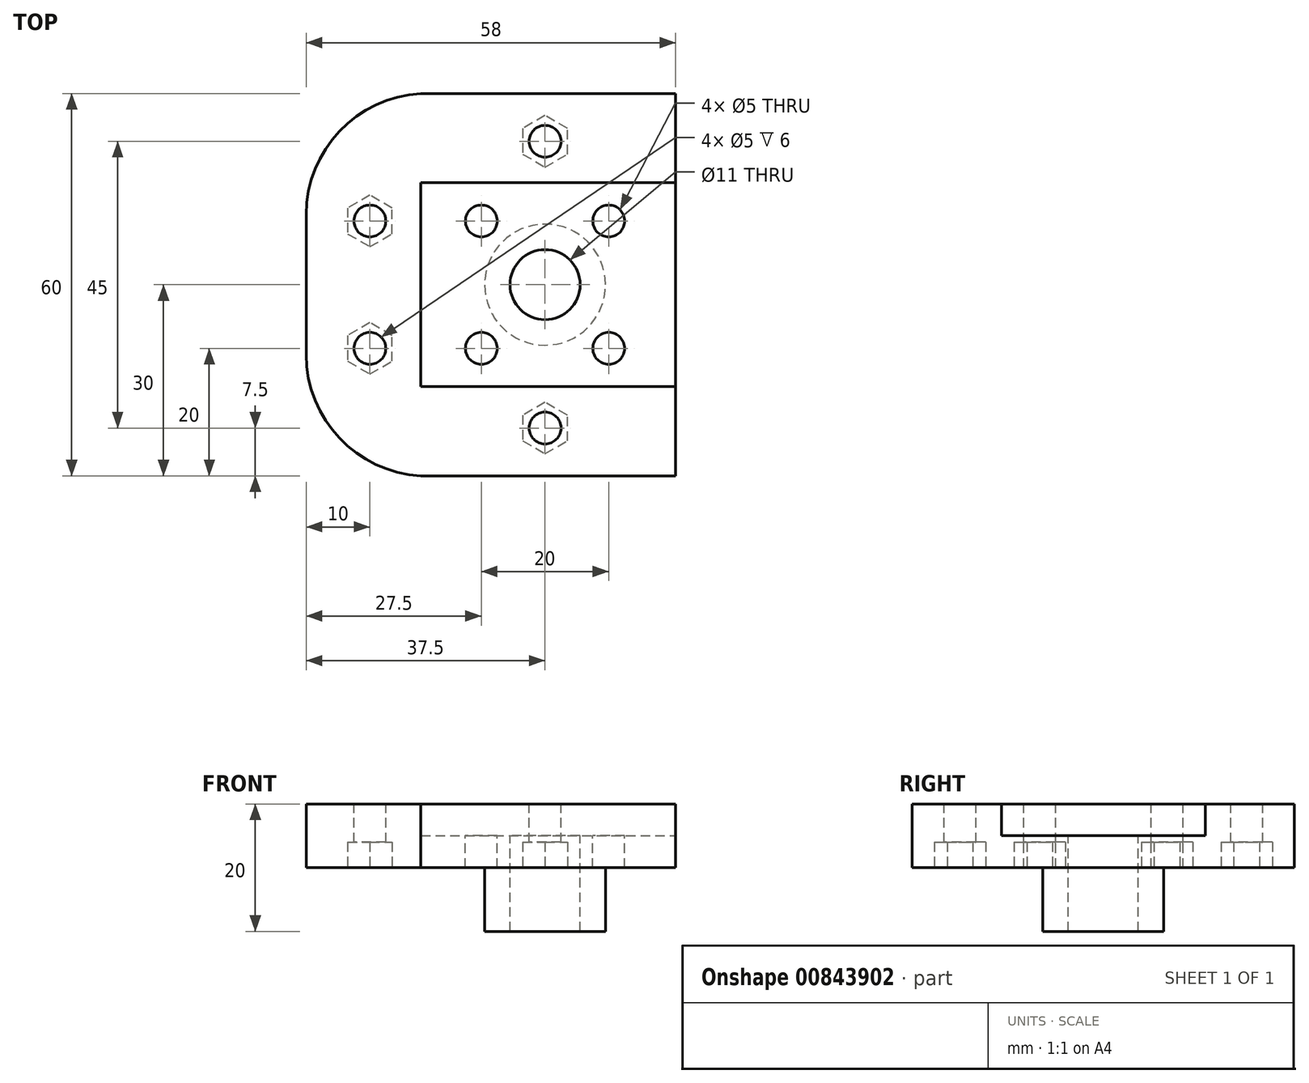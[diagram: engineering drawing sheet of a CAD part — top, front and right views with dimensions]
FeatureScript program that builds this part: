
annotation { "Feature Type Name" : "Feature", "Feature Type Description" : "" }
export const myFeature = defineFeature(function(context is Context, id is Id, definition is map)
    precondition{}
    {
        {
            var Q0;
            Q0=qCreatedBy(makeId("Top.planeOp"),FACE);
            var sketch = newSketch(context, id + "F0", { "sketchPlane" : qUnion([Q0])});
            skCircle(sketch, "E0", {"center": v(0, 0) * mm, "radius": 5.5 * mm});
            skCircle(sketch, "E1", {"center": v(-10, 10) * mm, "radius": 2.5 * mm});
            skCircle(sketch, "E2", {"center": v(10, 10) * mm, "radius": 2.5 * mm});
            skCircle(sketch, "E3", {"center": v(10, -10) * mm, "radius": 2.5 * mm});
            skCircle(sketch, "E4", {"center": v(-10, -10) * mm, "radius": 2.5 * mm});
            skLineSegment(sketch, "E5", {"start": v(-37.5, 11) * mm, "end": v(-37.5, -11) * mm});
            skPoint(sketch, "E6.orphan", {"position": v(-24, -15) * mm});
            skCircle(sketch, "E7", {"center": v(-27.5, 10) * mm, "radius": 2.5 * mm});
            skCircle(sketch, "E8", {"center": v(-27.5, -10) * mm, "radius": 2.5 * mm});
            skPoint(sketch, "E9.visualSharp", {"position": v(-37.5, 15) * mm});
            skPoint(sketch, "E10.visualSharp", {"position": v(-37.5, -15) * mm});
            skLineSegment(sketch, "E11", {"start": v(-19.5, 16) * mm, "end": v(-19.5, -16) * mm});
            skLineSegment(sketch, "E12", {"start": v(-19.5, -30) * mm, "end": v(20.5, -30) * mm});
            skLineSegment(sketch, "E13", {"start": v(-19.5, 30) * mm, "end": v(20.5, 30) * mm});
            skLineSegment(sketch, "E14", {"start": v(20.5, 30) * mm, "end": v(20.5, -30) * mm});
            skCircle(sketch, "E15", {"center": v(0, -22.5) * mm, "radius": 2.5 * mm});
            skCircle(sketch, "E16", {"center": v(0, 22.5) * mm, "radius": 2.5 * mm});
            skLineSegment(sketch, "E17", {"start": v(-19.5, 16) * mm, "end": v(20.5, 16) * mm});
            skArc(sketch, "E18", {"start": v(-37.5, 11) * mm, "mid": v(-32.29, 24.09) * mm, "end": v(-19.5, 30) * mm});
            skArc(sketch, "E19", {"start": v(-37.5, -11) * mm, "mid": v(-32.29, -24.09) * mm, "end": v(-19.5, -30) * mm});
            skLineSegment(sketch, "E20", {"start": v(-19.5, -16) * mm, "end": v(20.5, -16) * mm});
            skSolve(sketch);
        }
        {
            var Q0;
            Q0=makeQuery(id+"F0.imprint","IMPRINT",FACE,{"disambiguationData":[TD([[makeQuery(id+"F0.imprint","IMPRINT",EDGE,{"derivedFrom":sQuery(id+"F0.wireOp",EDGE,"E0")}),-1.0]])]});
            extrude(context, id + "F1", {"entities" : qUnion([Q0]), "oppositeDirection" : true, "depth" : 20 * mm, "offsetDistance" : 25 * mm});
        }
        {
            var Q0;
            Q0=makeQuery(id+"F0.imprint","IMPRINT",FACE,{"disambiguationData":[TD([[makeQuery(id+"F0.imprint","IMPRINT",EDGE,{"derivedFrom":sQuery(id+"F0.wireOp",EDGE,"E5")}),1.0]])]});
            extrude(context, id + "F2", {"entities" : qUnion([Q0]), "operationType" : NewBodyOperationType.ADD, "oppositeDirection" : true, "depth" : 10 * mm, "offsetDistance" : 25 * mm});
        }
        {
            var Q0;
            Q0=makeQuery(id+"F2.opExtrude","CAP_FACE",FACE,{"disambiguationData":[OSD([sQuery(id+"F0.wireOp",EDGE,"E5"),sQuery(id+"F0.wireOp",EDGE,"E7"),sQuery(id+"F0.wireOp",EDGE,"E8"),sQuery(id+"F0.wireOp",EDGE,"E11"),sQuery(id+"F0.wireOp",EDGE,"E12"),sQuery(id+"F0.wireOp",EDGE,"E13"),sQuery(id+"F0.wireOp",EDGE,"E14"),sQuery(id+"F0.wireOp",EDGE,"E15"),sQuery(id+"F0.wireOp",EDGE,"E16"),sQuery(id+"F0.wireOp",EDGE,"E17"),sQuery(id+"F0.wireOp",EDGE,"E18"),sQuery(id+"F0.wireOp",EDGE,"E19"),sQuery(id+"F0.wireOp",EDGE,"E20")])],"isStart":false});
            var sketch = newSketch(context, id + "F3", { "sketchPlane" : qUnion([Q0])});
            skCircle(sketch, "E21.cCircle", {"center": v(-27.5, 10) * mm, "radius": 3.5 * mm, "construction": true});
            skLineSegment(sketch, "E21.0", {"start": v(-24, 12.02) * mm, "end": v(-24, 7.98) * mm});
            skLineSegment(sketch, "E21.1", {"start": v(-24, 7.98) * mm, "end": v(-27.5, 5.96) * mm});
            skLineSegment(sketch, "E21.2", {"start": v(-27.5, 5.96) * mm, "end": v(-31, 7.98) * mm});
            skLineSegment(sketch, "E21.3", {"start": v(-31, 7.98) * mm, "end": v(-31, 12.02) * mm});
            skLineSegment(sketch, "E21.4", {"start": v(-31, 12.02) * mm, "end": v(-27.5, 14.04) * mm});
            skLineSegment(sketch, "E21.5", {"start": v(-27.5, 14.04) * mm, "end": v(-24, 12.02) * mm});
            skPoint(sketch, "E21.0.midPoint", {"position": v(-24, 10) * mm});
            skCircle(sketch, "E22.cCircle", {"center": v(-27.5, -10) * mm, "radius": 3.5 * mm, "construction": true});
            skLineSegment(sketch, "E22.0", {"start": v(-24, -7.98) * mm, "end": v(-24, -12.02) * mm});
            skLineSegment(sketch, "E22.1", {"start": v(-24, -12.02) * mm, "end": v(-27.5, -14.04) * mm});
            skLineSegment(sketch, "E22.2", {"start": v(-27.5, -14.04) * mm, "end": v(-31, -12.02) * mm});
            skLineSegment(sketch, "E22.3", {"start": v(-31, -12.02) * mm, "end": v(-31, -7.98) * mm});
            skLineSegment(sketch, "E22.4", {"start": v(-31, -7.98) * mm, "end": v(-27.5, -5.96) * mm});
            skLineSegment(sketch, "E22.5", {"start": v(-27.5, -5.96) * mm, "end": v(-24, -7.98) * mm});
            skPoint(sketch, "E22.0.midPoint", {"position": v(-24, -10) * mm});
            skCircle(sketch, "E23.cCircle", {"center": v(0, -22.5) * mm, "radius": 3.5 * mm, "construction": true});
            skLineSegment(sketch, "E23.0", {"start": v(3.5, -20.48) * mm, "end": v(3.5, -24.52) * mm});
            skLineSegment(sketch, "E23.1", {"start": v(3.5, -24.52) * mm, "end": v(0, -26.54) * mm});
            skLineSegment(sketch, "E23.2", {"start": v(0, -26.54) * mm, "end": v(-3.5, -24.52) * mm});
            skLineSegment(sketch, "E23.3", {"start": v(-3.5, -24.52) * mm, "end": v(-3.5, -20.48) * mm});
            skLineSegment(sketch, "E23.4", {"start": v(-3.5, -20.48) * mm, "end": v(0, -18.46) * mm});
            skLineSegment(sketch, "E23.5", {"start": v(0, -18.46) * mm, "end": v(3.5, -20.48) * mm});
            skPoint(sketch, "E23.0.midPoint", {"position": v(3.5, -22.5) * mm});
            skCircle(sketch, "E24.cCircle", {"center": v(0, 22.5) * mm, "radius": 3.5 * mm, "construction": true});
            skLineSegment(sketch, "E24.0", {"start": v(3.5, 24.52) * mm, "end": v(3.5, 20.48) * mm});
            skLineSegment(sketch, "E24.1", {"start": v(3.5, 20.48) * mm, "end": v(0, 18.46) * mm});
            skLineSegment(sketch, "E24.2", {"start": v(0, 18.46) * mm, "end": v(-3.5, 20.48) * mm});
            skLineSegment(sketch, "E24.3", {"start": v(-3.5, 20.48) * mm, "end": v(-3.5, 24.52) * mm});
            skLineSegment(sketch, "E24.4", {"start": v(-3.5, 24.52) * mm, "end": v(0, 26.54) * mm});
            skLineSegment(sketch, "E24.5", {"start": v(0, 26.54) * mm, "end": v(3.5, 24.52) * mm});
            skPoint(sketch, "E24.0.midPoint", {"position": v(3.5, 22.5) * mm});
            skSolve(sketch);
        }
        {
            var Q0;
            Q0=makeQuery(id+"F3.imprint","IMPRINT",FACE,{"disambiguationData":[TD([[makeQuery(id+"F3.imprint","IMPRINT",EDGE,{"derivedFrom":sQuery(id+"F3.wireOp",EDGE,"E24.0")}),-1.0]])]});
            var Q1;
            Q1=makeQuery(id+"F3.imprint","IMPRINT",FACE,{"disambiguationData":[TD([[makeQuery(id+"F3.imprint","IMPRINT",EDGE,{"derivedFrom":sQuery(id+"F3.wireOp",EDGE,"E21.0")}),-1.0]])]});
            var Q2;
            Q2=makeQuery(id+"F3.imprint","IMPRINT",FACE,{"disambiguationData":[TD([[makeQuery(id+"F3.imprint","IMPRINT",EDGE,{"derivedFrom":sQuery(id+"F3.wireOp",EDGE,"E23.0")}),-1.0]])]});
            var Q3;
            Q3=makeQuery(id+"F3.imprint","IMPRINT",FACE,{"disambiguationData":[TD([[makeQuery(id+"F3.imprint","IMPRINT",EDGE,{"derivedFrom":sQuery(id+"F3.wireOp",EDGE,"E22.0")}),-1.0]])]});
            extrude(context, id + "F4", {"entities" : qUnion([Q0, Q1, Q2, Q3]), "operationType" : NewBodyOperationType.REMOVE, "oppositeDirection" : true, "depth" : 4 * mm, "offsetDistance" : 25 * mm});
        }
        {
            var Q0;
            Q0=makeQuery(id+"F1.opExtrude","CAP_FACE",FACE,{"disambiguationData":[OSD([sQuery(id+"F0.wireOp",EDGE,"E0"),sQuery(id+"F0.wireOp",EDGE,"E1"),sQuery(id+"F0.wireOp",EDGE,"E2"),sQuery(id+"F0.wireOp",EDGE,"E3"),sQuery(id+"F0.wireOp",EDGE,"E4"),sQuery(id+"F0.wireOp",EDGE,"E11"),sQuery(id+"F0.wireOp",EDGE,"E14"),sQuery(id+"F0.wireOp",EDGE,"E17"),sQuery(id+"F0.wireOp",EDGE,"E20")])],"isStart":false});
            var sketch = newSketch(context, id + "F5", { "sketchPlane" : qUnion([Q0])});
            skCircle(sketch, "E25", {"center": v(0, 0) * mm, "radius": 9.5 * mm});
            skSolve(sketch);
        }
        {
            var Q0;
            Q0=makeQuery(id+"F5.imprint","IMPRINT",FACE,{"disambiguationData":[TD([[makeQuery(id+"F5.imprint","IMPRINT",EDGE,{"derivedFrom":sQuery(id+"F5.wireOp",EDGE,"E25")}),-1.0]])]});
            extrude(context, id + "F6", {"entities" : qUnion([Q0]), "operationType" : NewBodyOperationType.REMOVE, "oppositeDirection" : true, "depth" : 10 * mm, "offsetDistance" : 25 * mm});
        }
        {
            var Q0;
            Q0=makeQuery(id+"F0.imprint","IMPRINT",FACE,{"disambiguationData":[TD([[makeQuery(id+"F0.imprint","IMPRINT",EDGE,{"derivedFrom":sQuery(id+"F0.wireOp",EDGE,"E0")}),-1.0]])]});
            extrude(context, id + "F7", {"entities" : qUnion([Q0]), "operationType" : NewBodyOperationType.REMOVE, "oppositeDirection" : true, "depth" : 5 * mm, "offsetDistance" : 25 * mm});
        }
    });
